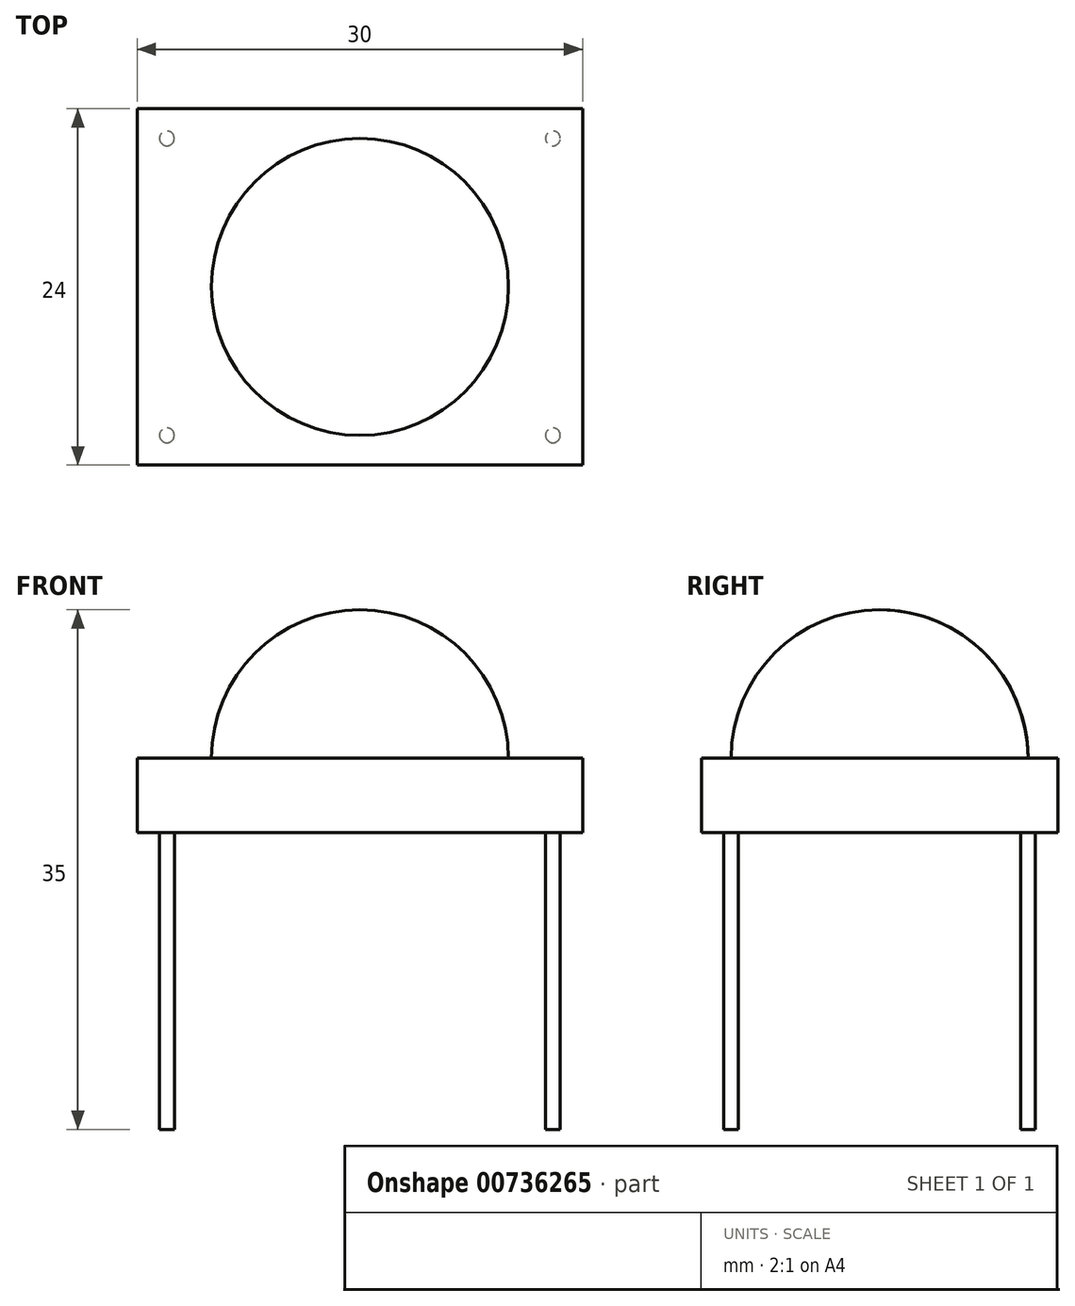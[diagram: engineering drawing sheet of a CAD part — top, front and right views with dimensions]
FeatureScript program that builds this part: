
annotation { "Feature Type Name" : "Feature", "Feature Type Description" : "" }
export const myFeature = defineFeature(function(context is Context, id is Id, definition is map)
    precondition{}
    {
        {
            var Q0;
            Q0=qCreatedBy(makeId("Top.planeOp"),FACE);
            var sketch = newSketch(context, id + "F0", { "sketchPlane" : qUnion([Q0])});
            skLineSegment(sketch, "E0.bottom", {"start": v(-15, 12) * mm, "end": v(15, 12) * mm});
            skLineSegment(sketch, "E0.top", {"start": v(-15, -12) * mm, "end": v(15, -12) * mm});
            skLineSegment(sketch, "E0.left", {"start": v(-15, 12) * mm, "end": v(-15, -12) * mm});
            skLineSegment(sketch, "E0.right", {"start": v(15, 12) * mm, "end": v(15, -12) * mm});
            skLineSegment(sketch, "E1", {"start": v(-15, -12) * mm, "end": v(15, 12) * mm, "construction": true});
            skPoint(sketch, "E2", {"position": v(0, 0) * mm});
            skSolve(sketch);
        }
        {
            var Q0;
            Q0=makeQuery(id+"F0.imprint","IMPRINT",FACE,{"disambiguationData":[TD([[makeQuery(id+"F0.imprint","IMPRINT",EDGE,{"derivedFrom":sQuery(id+"F0.wireOp",EDGE,"E0.bottom")}),-1.0]])]});
            extrude(context, id + "F1", {"entities" : qUnion([Q0]), "oppositeDirection" : true, "depth" : 5 * mm, "offsetDistance" : 25 * mm});
        }
        {
            var Q0;
            Q0=qCreatedBy(makeId("Right.planeOp"),FACE);
            var sketch = newSketch(context, id + "F2", { "sketchPlane" : qUnion([Q0])});
            skLineSegment(sketch, "E3", {"start": v(0, 0) * mm, "end": v(0, 10) * mm});
            skLineSegment(sketch, "E4", {"start": v(0, 0) * mm, "end": v(10, 0) * mm});
            skArc(sketch, "E5", {"start": v(0, 10) * mm, "mid": v(7.07, 7.07) * mm, "end": v(10, 0) * mm});
            skSolve(sketch);
        }
        {
            var Q0;
            Q0=makeQuery(id+"F2.imprint","IMPRINT",FACE,{"disambiguationData":[TD([[makeQuery(id+"F2.imprint","IMPRINT",EDGE,{"derivedFrom":sQuery(id+"F2.wireOp",EDGE,"E3")}),-1.0]])]});
            var Q1;
            Q1=sQuery(id+"F2.wireOp",EDGE,"E3");
            revolve(context, id + "F3", {"surfaceOperationType" : NewSurfaceOperationType.NEW, "entities" : qUnion([Q0]), "axis" : qUnion([Q1]), "revolveType" : RevolveType.FULL});
        }
        {
            var Q0;
            Q0=makeQuery(id+"F1.opExtrude","CAP_FACE",FACE,{"disambiguationData":[OSD([sQuery(id+"F0.wireOp",EDGE,"E0.bottom"),sQuery(id+"F0.wireOp",EDGE,"E0.top"),sQuery(id+"F0.wireOp",EDGE,"E0.left"),sQuery(id+"F0.wireOp",EDGE,"E0.right")])],"isStart":false});
            var sketch = newSketch(context, id + "F4", { "sketchPlane" : qUnion([Q0])});
            skCircle(sketch, "E6", {"center": v(13, -10) * mm, "radius": 0.5 * mm});
            skLineSegment(sketch, "E7", {"start": v(15, -10) * mm, "end": v(13, -10) * mm});
            skLineSegment(sketch, "E8", {"start": v(13, -12) * mm, "end": v(13, -10) * mm});
            skCircle(sketch, "E9.0.1.0", {"center": v(13, 10) * mm, "radius": 0.5 * mm});
            skCircle(sketch, "E9.1.0.0", {"center": v(-13, -10) * mm, "radius": 0.5 * mm});
            skCircle(sketch, "E9.1.1.0", {"center": v(-13, 10) * mm, "radius": 0.5 * mm});
            skLineSegment(sketch, "E9.direction1", {"start": v(13, -10) * mm, "end": v(-13, -10) * mm, "construction": true});
            skLineSegment(sketch, "E9.direction2", {"start": v(13, -10) * mm, "end": v(13, 10) * mm, "construction": true});
            skSolve(sketch);
        }
        {
            var Q0;
            Q0 = qSketchRegion(id + "F4", true);
            extrude(context, id + "F5", {"entities" : qUnion([Q0]), "operationType" : NewBodyOperationType.ADD, "depth" : 20 * mm, "offsetDistance" : 25 * mm});
        }
    });
